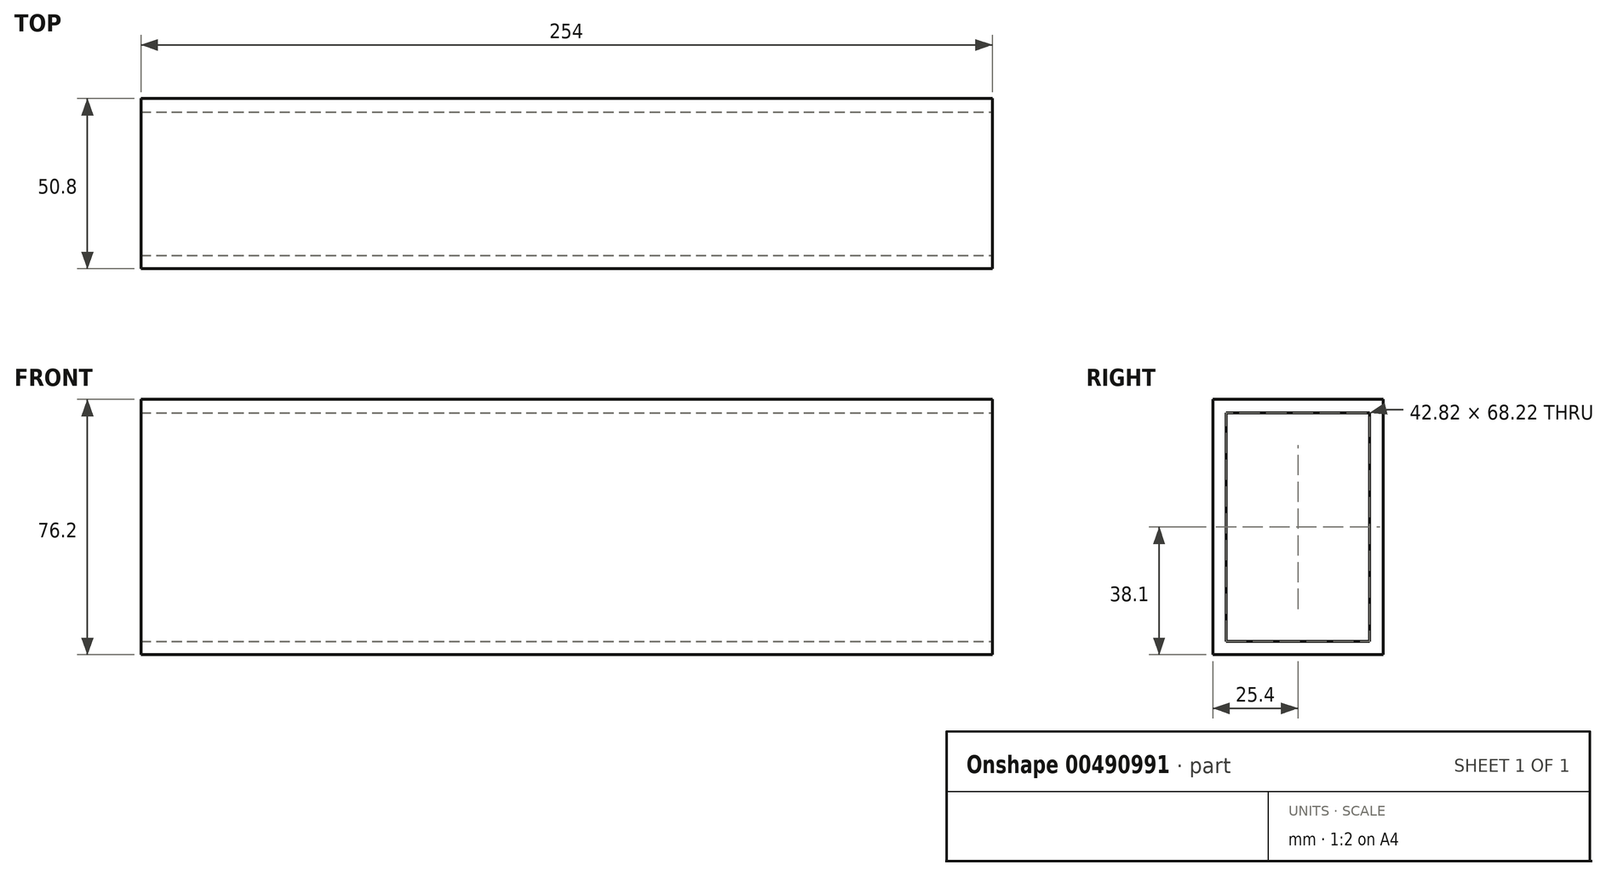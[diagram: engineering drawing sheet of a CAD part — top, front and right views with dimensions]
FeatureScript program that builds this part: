
annotation { "Feature Type Name" : "Feature", "Feature Type Description" : "" }
export const myFeature = defineFeature(function(context is Context, id is Id, definition is map)
    precondition{}
    {
        {
            var Q0;
            Q0=qCreatedBy(makeId("Top.planeOp"),FACE);
            var sketch = newSketch(context, id + "F0", { "sketchPlane" : qUnion([Q0])});
            skLineSegment(sketch, "E0.bottom", {"start": v(0, 0) * mm, "end": v(254, 0) * mm});
            skLineSegment(sketch, "E0.top", {"start": v(0, 50.8) * mm, "end": v(254, 50.8) * mm});
            skLineSegment(sketch, "E0.left", {"start": v(0, 0) * mm, "end": v(0, 50.8) * mm});
            skLineSegment(sketch, "E0.right", {"start": v(254, 0) * mm, "end": v(254, 50.8) * mm});
            skSolve(sketch);
        }
        {
            var Q0;
            Q0=makeQuery(id+"F0.imprint","IMPRINT",FACE,{"disambiguationData":[TD([[makeQuery(id+"F0.imprint","IMPRINT",EDGE,{"derivedFrom":sQuery(id+"F0.wireOp",EDGE,"E0.bottom")}),1.0]])]});
            extrude(context, id + "F1", {"entities" : qUnion([Q0]), "depth" : 76.2 * mm});
        }
        {
            var Q0;
            Q0=makeQuery(id+"F1.opExtrude","SWEPT_FACE",FACE,{"disambiguationData":[OSD([sQuery(id+"F0.wireOp",EDGE,"E0.right")])]});
            shell(context, id + "F2", {"entities" : qUnion([Q0]), "thickness" : 4 * mm});
        }
        {
            var Q0;
            Q0=makeQuery(id+"F2.opShell","OFFSET_FACE",FACE,{"disambiguationData":[OSD([sQuery(id+"F0.wireOp",EDGE,"E0.left")])]});
            extrude(context, id + "F3", {"entities" : qUnion([Q0]), "operationType" : NewBodyOperationType.REMOVE, "endBound" : BoundingType.THROUGH_ALL, "oppositeDirection" : true, "depth" : 25.4 * mm});
        }
    });
